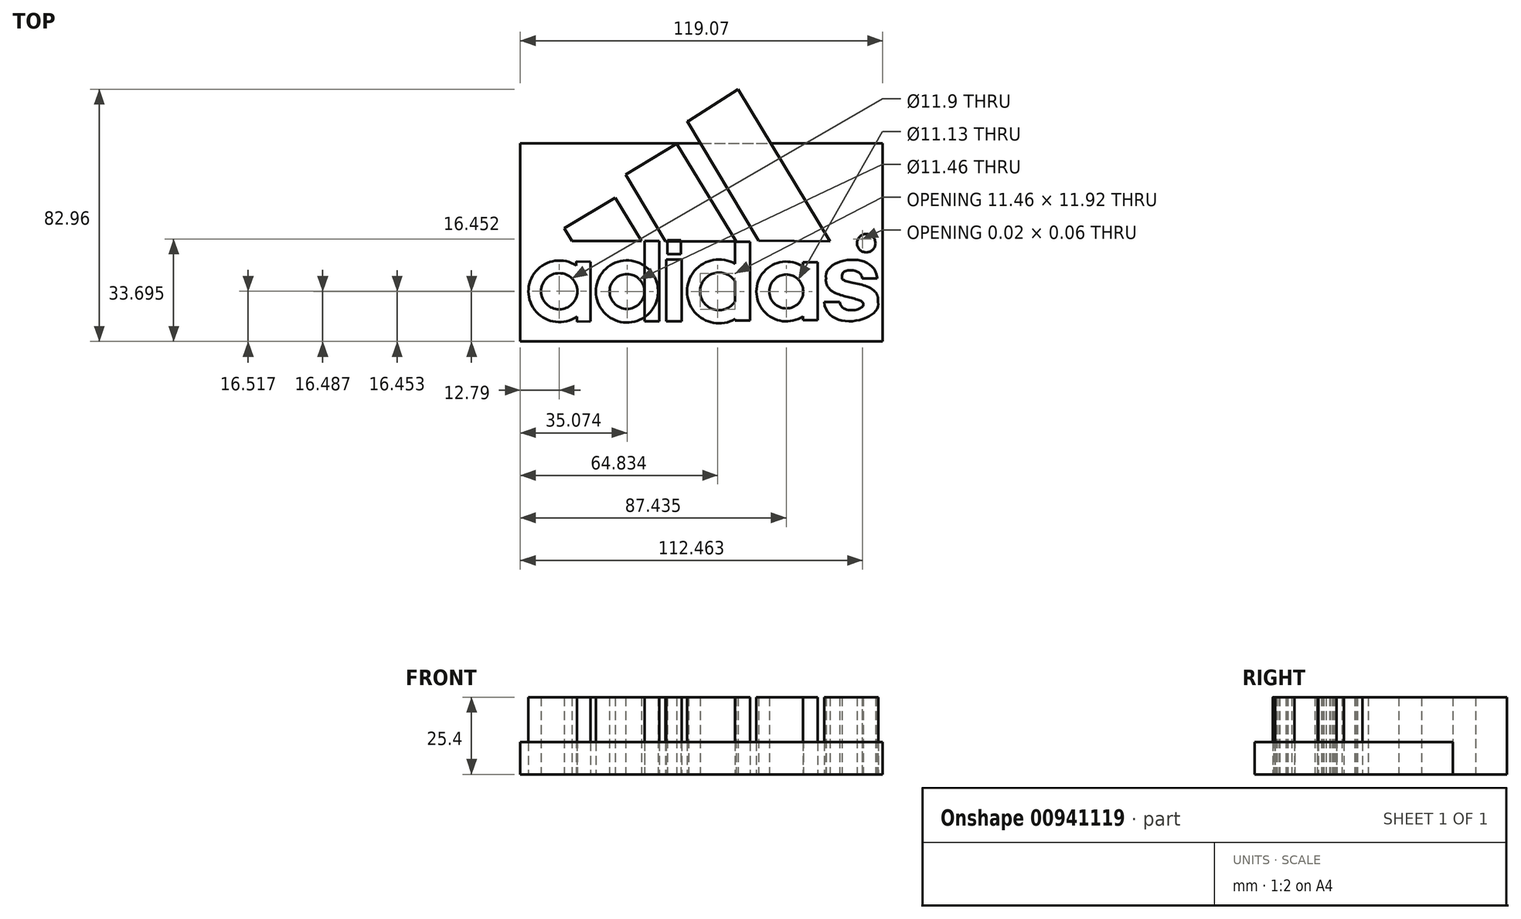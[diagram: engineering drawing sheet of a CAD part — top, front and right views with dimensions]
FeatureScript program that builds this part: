
annotation { "Feature Type Name" : "Feature", "Feature Type Description" : "" }
export const myFeature = defineFeature(function(context is Context, id is Id, definition is map)
    precondition{}
    {
        {
            var Q0;
            Q0=qCreatedBy(makeId("Top.planeOp"),FACE);
            var sketch = newSketch(context, id + "F0", { "sketchPlane" : qUnion([Q0])});
            skLineSegment(sketch, "E0", {"start": v(-39.48, 7.07) * mm, "end": v(-36.94, 2.8) * mm});
            skLineSegment(sketch, "E1", {"start": v(-36.94, 2.8) * mm, "end": v(-14.13, 2.8) * mm});
            skLineSegment(sketch, "E2", {"start": v(-14.13, 2.8) * mm, "end": v(-22.77, 17.1) * mm});
            skCircle(sketch, "E3", {"center": v(-41.14, -13.7) * mm, "radius": 10.12 * mm});
            skCircle(sketch, "E4", {"center": v(-18.86, -13.76) * mm, "radius": 10.22 * mm});
            skLineSegment(sketch, "E5", {"start": v(-22.77, 17.1) * mm, "end": v(-39.48, 7.07) * mm});
            skLineSegment(sketch, "E6", {"start": v(-19.29, 24.7) * mm, "end": v(-6.25, 2.78) * mm});
            skLineSegment(sketch, "E7", {"start": v(-6.25, 2.78) * mm, "end": v(16.96, 2.78) * mm});
            skLineSegment(sketch, "E8", {"start": v(16.96, 2.78) * mm, "end": v(-2.5, 34.87) * mm});
            skLineSegment(sketch, "E9", {"start": v(-2.5, 34.87) * mm, "end": v(-19.29, 24.7) * mm});
            skLineSegment(sketch, "E10", {"start": v(0.86, 42.38) * mm, "end": v(24.36, 2.98) * mm});
            skLineSegment(sketch, "E11", {"start": v(24.36, 2.98) * mm, "end": v(47.87, 2.68) * mm});
            skLineSegment(sketch, "E12", {"start": v(47.87, 2.68) * mm, "end": v(17.65, 52.75) * mm});
            skLineSegment(sketch, "E13", {"start": v(17.65, 52.75) * mm, "end": v(1.35, 42.38) * mm});
            skLineSegment(sketch, "E14", {"start": v(-13.03, -23.52) * mm, "end": v(-13.03, 2.8) * mm});
            skLineSegment(sketch, "E15", {"start": v(-13.03, 2.8) * mm, "end": v(-8.21, 2.8) * mm});
            skLineSegment(sketch, "E16", {"start": v(-8.21, 2.8) * mm, "end": v(-8.21, -23.6) * mm});
            skLineSegment(sketch, "E17", {"start": v(-8.21, -23.6) * mm, "end": v(-13.03, -23.52) * mm});
            skLineSegment(sketch, "E18", {"start": v(-35.53, -3.92) * mm, "end": v(-30.88, -4) * mm});
            skLineSegment(sketch, "E19", {"start": v(-30.88, -4) * mm, "end": v(-30.88, -23.52) * mm});
            skLineSegment(sketch, "E20", {"start": v(-30.88, -23.52) * mm, "end": v(-35.36, -23.65) * mm});
            skLineSegment(sketch, "E21", {"start": v(-35.36, -23.65) * mm, "end": v(-35.53, -3.92) * mm});
            skCircle(sketch, "E22", {"center": v(11.37, -13.72) * mm, "radius": 10.5 * mm});
            skLineSegment(sketch, "E23.bottom", {"start": v(21.61, 2.66) * mm, "end": v(16.63, 2.66) * mm});
            skLineSegment(sketch, "E23.top", {"start": v(21.61, -23.35) * mm, "end": v(16.63, -23.35) * mm});
            skLineSegment(sketch, "E23.left", {"start": v(21.61, 2.66) * mm, "end": v(21.61, -23.35) * mm});
            skLineSegment(sketch, "E23.right", {"start": v(16.63, 2.66) * mm, "end": v(16.63, -23.35) * mm});
            skCircle(sketch, "E24", {"center": v(33.5, -13.76) * mm, "radius": 9.83 * mm});
            skLineSegment(sketch, "E25.bottom", {"start": v(43.8, -4.13) * mm, "end": v(39, -4.13) * mm});
            skLineSegment(sketch, "E25.top", {"start": v(43.8, -23.18) * mm, "end": v(39, -23.18) * mm});
            skLineSegment(sketch, "E25.left", {"start": v(43.8, -4.13) * mm, "end": v(43.8, -23.18) * mm});
            skLineSegment(sketch, "E25.right", {"start": v(39, -4.13) * mm, "end": v(39, -23.18) * mm});
            skLineSegment(sketch, "E26.bottom", {"start": v(-5.57, 3.16) * mm, "end": v(-1.1, 3.16) * mm});
            skLineSegment(sketch, "E26.top", {"start": v(-5.57, -1.48) * mm, "end": v(-1.1, -1.48) * mm});
            skLineSegment(sketch, "E26.left", {"start": v(-5.57, 3.16) * mm, "end": v(-5.57, -1.48) * mm});
            skLineSegment(sketch, "E26.right", {"start": v(-1.1, 3.16) * mm, "end": v(-1.1, -1.48) * mm});
            skFitSpline(sketch, "E27", {"points": [v(63.31, -9.23) * mm, v(46.55, -9.6) * mm], "startDerivative": vector(-1.82, 27.46) * mm, "endDerivative": vector(4.32, -20.97) * mm});
            skFitSpline(sketch, "E28", {"points": [v(46.55, -9.6) * mm, v(58.8, -18) * mm], "startDerivative": vector(-1.87, -20.55) * mm, "endDerivative": vector(-0.15, -8.89) * mm});
            skFitSpline(sketch, "E29", {"points": [v(58.8, -18) * mm, v(51.07, -17.18) * mm], "startDerivative": vector(-0.5, -6.81) * mm, "endDerivative": vector(-0.92, 11.9) * mm});
            skLineSegment(sketch, "E30", {"start": v(51.07, -17.18) * mm, "end": v(45.92, -17.18) * mm});
            skFitSpline(sketch, "E31", {"points": [v(45.92, -17.18) * mm, v(63.62, -17.18) * mm], "startDerivative": vector(3.22, -31.3) * mm, "endDerivative": vector(-5.1, 18.8) * mm});
            skFitSpline(sketch, "E32", {"points": [v(63.62, -17.18) * mm, v(51.81, -9.24) * mm], "startDerivative": vector(2.68, 21.03) * mm, "endDerivative": vector(0.68, 6.95) * mm});
            skFitSpline(sketch, "E33", {"points": [v(51.81, -9.24) * mm, v(58.4, -9.48) * mm], "startDerivative": vector(-2.42, 10.76) * mm, "endDerivative": vector(-0.35, -10.04) * mm});
            skLineSegment(sketch, "E34", {"start": v(58.4, -9.48) * mm, "end": v(63.31, -9.48) * mm});
            skCircle(sketch, "E35", {"center": v(-41.14, -13.7) * mm, "radius": 5.95 * mm});
            skCircle(sketch, "E36", {"center": v(-61.96, 49.8) * mm, "radius": 8.9 * mm});
            skCircle(sketch, "E37", {"center": v(-18.86, -13.76) * mm, "radius": 5.73 * mm});
            skCircle(sketch, "E38", {"center": v(11.37, -13.72) * mm, "radius": 6.2 * mm});
            skCircle(sketch, "E39", {"center": v(33.5, -13.76) * mm, "radius": 5.57 * mm});
            skLineSegment(sketch, "E40", {"start": v(-41.14, -13.7) * mm, "end": v(73.81, -13.76) * mm});
            skLineSegment(sketch, "E41.bottom", {"start": v(-5.96, -3.28) * mm, "end": v(-0.9, -3.28) * mm});
            skLineSegment(sketch, "E41.top", {"start": v(-5.96, -23.55) * mm, "end": v(-0.9, -23.55) * mm});
            skLineSegment(sketch, "E41.left", {"start": v(-5.96, -3.28) * mm, "end": v(-5.96, -23.55) * mm});
            skLineSegment(sketch, "E41.right", {"start": v(-0.9, -3.28) * mm, "end": v(-0.9, -23.55) * mm});
            skCircle(sketch, "E42", {"center": v(59.77, 2.13) * mm, "radius": 3.03 * mm});
            skLineSegment(sketch, "E43", {"start": v(58.54, 0.35) * mm, "end": v(58.54, 3.52) * mm});
            skFitSpline(sketch, "E44", {"points": [v(58.54, 3.52) * mm, v(61.1, 2.56) * mm], "startDerivative": vector(-0.9, -0.98) * mm, "endDerivative": vector(-0.71, -4.78) * mm});
            skFitSpline(sketch, "E45", {"points": [v(61.1, 2.56) * mm, v(60.32, 1.72) * mm], "startDerivative": vector(-0.12, -0.78) * mm, "endDerivative": vector(-1.35, -0.31) * mm});
            skLineSegment(sketch, "E46", {"start": v(60.32, 1.72) * mm, "end": v(61.34, 0.36) * mm});
            skLineSegment(sketch, "E47", {"start": v(61.34, 0.36) * mm, "end": v(60.62, 0.36) * mm});
            skLineSegment(sketch, "E48", {"start": v(60.62, 0.36) * mm, "end": v(59.84, 1.57) * mm});
            skLineSegment(sketch, "E49", {"start": v(59.84, 1.57) * mm, "end": v(59.1, 1.57) * mm});
            skLineSegment(sketch, "E50", {"start": v(59.1, 1.57) * mm, "end": v(59.1, 0.34) * mm});
            skLineSegment(sketch, "E51", {"start": v(59.1, 0.34) * mm, "end": v(58.54, 0.35) * mm});
            skLineSegment(sketch, "E52", {"start": v(59.18, 2.97) * mm, "end": v(59.18, 2.3) * mm});
            skLineSegment(sketch, "E53", {"start": v(59.18, 2.3) * mm, "end": v(60.21, 2.3) * mm});
            skFitSpline(sketch, "E54", {"points": [v(60.21, 2.3) * mm, v(60.21, 2.98) * mm], "startDerivative": vector(0.84, 0.17) * mm, "endDerivative": vector(-1.16, 0.41) * mm});
            skLineSegment(sketch, "E55", {"start": v(59.18, 2.97) * mm, "end": v(60.21, 2.98) * mm});
            skLineSegment(sketch, "E56", {"start": v(63.31, -9.23) * mm, "end": v(63.31, -9.48) * mm});
            skLineSegment(sketch, "E57", {"start": v(1.35, 42.38) * mm, "end": v(0.86, 42.38) * mm});
            skSolve(sketch);
        }
        {
            var Q0;
            {var subQ0=sQuery(id+"F0.wireOp",EDGE,"E20");Q0=makeQuery(id+"F0.imprint","IMPRINT",FACE,{"disambiguationData":[TD([[makeQuery(id+"F0.imprint","IMPRINT",EDGE,{"derivedFrom":subQ0}),-1.0]])]});}
            var Q1;
            {var subQ0=sQuery(id+"F0.wireOp",EDGE,"E40");var subQ1=sQuery(id+"F0.wireOp",EDGE,"E4");var subQ2=makeQuery(id+"F0.imprint","INTERSECT",VERTEX,{"disambiguationData":[OD(0.0)],"derivedFrom":[subQ1,subQ0]});Q1=makeQuery(id+"F0.imprint","IMPRINT",FACE,{"disambiguationData":[TD([[makeQuery(id+"F0.imprint","IMPRINT",EDGE,{"disambiguationData":[TD([[subQ2,-1.0]])],"derivedFrom":subQ1}),1.0]])]});}
            var Q2;
            {var subQ5=sQuery(id+"F0.wireOp",EDGE,"E41.top");Q2=makeQuery(id+"F0.imprint","IMPRINT",FACE,{"disambiguationData":[TD([[makeQuery(id+"F0.imprint","IMPRINT",EDGE,{"derivedFrom":subQ5}),1.0]])]});}
            var Q3;
            {var subQ5=sQuery(id+"F0.wireOp",EDGE,"E41.bottom");Q3=makeQuery(id+"F0.imprint","IMPRINT",FACE,{"disambiguationData":[TD([[makeQuery(id+"F0.imprint","IMPRINT",EDGE,{"derivedFrom":subQ5}),-1.0]])]});}
            var Q4;
            {var subQ5=sQuery(id+"F0.wireOp",EDGE,"E26.top");Q4=makeQuery(id+"F0.imprint","IMPRINT",FACE,{"disambiguationData":[TD([[makeQuery(id+"F0.imprint","IMPRINT",EDGE,{"derivedFrom":subQ5}),1.0]])]});}
            var Q5;
            {var subQ0=sQuery(id+"F0.wireOp",EDGE,"E40");var subQ1=sQuery(id+"F0.wireOp",EDGE,"E22");var subQ2=makeQuery(id+"F0.imprint","INTERSECT",VERTEX,{"disambiguationData":[OD(0.0)],"derivedFrom":[subQ1,subQ0]});Q5=makeQuery(id+"F0.imprint","IMPRINT",FACE,{"disambiguationData":[TD([[makeQuery(id+"F0.imprint","IMPRINT",EDGE,{"disambiguationData":[TD([[subQ2,1.0]])],"derivedFrom":subQ1}),1.0]])]});}
            var Q6;
            {var subQ0=sQuery(id+"F0.wireOp",EDGE,"E40");var subQ1=sQuery(id+"F0.wireOp",EDGE,"E22");var subQ2=makeQuery(id+"F0.imprint","INTERSECT",VERTEX,{"disambiguationData":[OD(0.0)],"derivedFrom":[subQ1,subQ0]});Q6=makeQuery(id+"F0.imprint","IMPRINT",FACE,{"disambiguationData":[TD([[makeQuery(id+"F0.imprint","IMPRINT",EDGE,{"disambiguationData":[TD([[subQ2,-1.0]])],"derivedFrom":subQ1}),1.0]])]});}
            var Q7;
            {var subQ1=sQuery(id+"F0.wireOp",EDGE,"E23.right");var subQ5=sQuery(id+"F0.wireOp",EDGE,"E22");var subQ6=makeQuery(id+"F0.imprint","INTERSECT",VERTEX,{"disambiguationData":[OD(1.0)],"derivedFrom":[subQ5,subQ1]});Q7=makeQuery(id+"F0.imprint","IMPRINT",FACE,{"disambiguationData":[TD([[makeQuery(id+"F0.imprint","IMPRINT",EDGE,{"disambiguationData":[TD([[subQ6,-1.0]])],"derivedFrom":subQ5}),1.0]])]});}
            var Q8;
            {var subQ1=sQuery(id+"F0.wireOp",EDGE,"E23.right");var subQ5=sQuery(id+"F0.wireOp",EDGE,"E22");var subQ6=makeQuery(id+"F0.imprint","INTERSECT",VERTEX,{"disambiguationData":[OD(0.0)],"derivedFrom":[subQ5,subQ1]});Q8=makeQuery(id+"F0.imprint","IMPRINT",FACE,{"disambiguationData":[TD([[makeQuery(id+"F0.imprint","IMPRINT",EDGE,{"disambiguationData":[TD([[subQ6,1.0]])],"derivedFrom":subQ5}),1.0]])]});}
            var Q9;
            {var subQ5=sQuery(id+"F0.wireOp",EDGE,"E23.bottom");Q9=makeQuery(id+"F0.imprint","IMPRINT",FACE,{"disambiguationData":[TD([[makeQuery(id+"F0.imprint","IMPRINT",EDGE,{"derivedFrom":subQ5}),1.0]])]});}
            var Q10;
            {var subQ5=sQuery(id+"F0.wireOp",EDGE,"E23.top");Q10=makeQuery(id+"F0.imprint","IMPRINT",FACE,{"disambiguationData":[TD([[makeQuery(id+"F0.imprint","IMPRINT",EDGE,{"derivedFrom":subQ5}),-1.0]])]});}
            var Q11;
            {var subQ0=sQuery(id+"F0.wireOp",EDGE,"E38");var subQ1=sQuery(id+"F0.wireOp",EDGE,"E23.right");var subQ2=makeQuery(id+"F0.imprint","INTERSECT",VERTEX,{"disambiguationData":[OD(0.0)],"derivedFrom":[subQ1,subQ0]});Q11=makeQuery(id+"F0.imprint","IMPRINT",FACE,{"disambiguationData":[TD([[makeQuery(id+"F0.imprint","IMPRINT",EDGE,{"disambiguationData":[TD([[subQ2,-1.0]])],"derivedFrom":subQ1}),1.0]])]});}
            var Q12;
            {var subQ0=sQuery(id+"F0.wireOp",EDGE,"E40");var subQ1=sQuery(id+"F0.wireOp",EDGE,"E23.right");var subQ2=makeQuery(id+"F0.imprint","INTERSECT",VERTEX,{"derivedFrom":[subQ1,subQ0]});Q12=makeQuery(id+"F0.imprint","IMPRINT",FACE,{"disambiguationData":[TD([[makeQuery(id+"F0.imprint","IMPRINT",EDGE,{"disambiguationData":[TD([[subQ2,-1.0]])],"derivedFrom":subQ1}),1.0]])]});}
            var Q13;
            {var subQ0=sQuery(id+"F0.wireOp",EDGE,"E40");var subQ1=sQuery(id+"F0.wireOp",EDGE,"E24");var subQ2=makeQuery(id+"F0.imprint","INTERSECT",VERTEX,{"disambiguationData":[OD(0.0)],"derivedFrom":[subQ1,subQ0]});Q13=makeQuery(id+"F0.imprint","IMPRINT",FACE,{"disambiguationData":[TD([[makeQuery(id+"F0.imprint","IMPRINT",EDGE,{"disambiguationData":[TD([[subQ2,1.0]])],"derivedFrom":subQ1}),1.0]])]});}
            var Q14;
            {var subQ0=sQuery(id+"F0.wireOp",EDGE,"E25.right");var subQ1=sQuery(id+"F0.wireOp",EDGE,"E24");var subQ2=makeQuery(id+"F0.imprint","INTERSECT",VERTEX,{"disambiguationData":[OD(0.0)],"derivedFrom":[subQ1,subQ0]});Q14=makeQuery(id+"F0.imprint","IMPRINT",FACE,{"disambiguationData":[TD([[makeQuery(id+"F0.imprint","IMPRINT",EDGE,{"disambiguationData":[TD([[subQ2,1.0]])],"derivedFrom":subQ1}),1.0]])]});}
            var Q15;
            {var subQ0=sQuery(id+"F0.wireOp",EDGE,"E25.right");var subQ1=sQuery(id+"F0.wireOp",EDGE,"E24");var subQ2=makeQuery(id+"F0.imprint","INTERSECT",VERTEX,{"disambiguationData":[OD(1.0)],"derivedFrom":[subQ1,subQ0]});Q15=makeQuery(id+"F0.imprint","IMPRINT",FACE,{"disambiguationData":[TD([[makeQuery(id+"F0.imprint","IMPRINT",EDGE,{"disambiguationData":[TD([[subQ2,-1.0]])],"derivedFrom":subQ1}),1.0]])]});}
            var Q16;
            {var subQ0=sQuery(id+"F0.wireOp",EDGE,"E40");var subQ1=sQuery(id+"F0.wireOp",EDGE,"E24");var subQ2=makeQuery(id+"F0.imprint","INTERSECT",VERTEX,{"disambiguationData":[OD(0.0)],"derivedFrom":[subQ1,subQ0]});Q16=makeQuery(id+"F0.imprint","IMPRINT",FACE,{"disambiguationData":[TD([[makeQuery(id+"F0.imprint","IMPRINT",EDGE,{"disambiguationData":[TD([[subQ2,-1.0]])],"derivedFrom":subQ1}),1.0]])]});}
            var Q17;
            {var subQ1=sQuery(id+"F0.wireOp",EDGE,"E25.top");Q17=makeQuery(id+"F0.imprint","IMPRINT",FACE,{"disambiguationData":[TD([[makeQuery(id+"F0.imprint","IMPRINT",EDGE,{"derivedFrom":subQ1}),-1.0]])]});}
            var Q18;
            {var subQ1=sQuery(id+"F0.wireOp",EDGE,"E25.bottom");Q18=makeQuery(id+"F0.imprint","IMPRINT",FACE,{"disambiguationData":[TD([[makeQuery(id+"F0.imprint","IMPRINT",EDGE,{"derivedFrom":subQ1}),1.0]])]});}
            var Q19;
            {var subQ1=sQuery(id+"F0.wireOp",EDGE,"E29");Q19=makeQuery(id+"F0.imprint","IMPRINT",FACE,{"disambiguationData":[TD([[makeQuery(id+"F0.imprint","IMPRINT",EDGE,{"derivedFrom":subQ1}),1.0]])]});}
            var Q20;
            {var subQ7=sQuery(id+"F0.wireOp",EDGE,"E6");Q20=makeQuery(id+"F0.imprint","IMPRINT",FACE,{"disambiguationData":[TD([[makeQuery(id+"F0.imprint","IMPRINT",EDGE,{"derivedFrom":subQ7}),1.0]])]});}
            var Q21;
            Q21=makeQuery(id+"F0.imprint","IMPRINT",FACE,{"disambiguationData":[TD([[makeQuery(id+"F0.imprint","IMPRINT",EDGE,{"derivedFrom":sQuery(id+"F0.wireOp",EDGE,"E0")}),1.0]])]});
            var Q22;
            Q22=makeQuery(id+"F0.imprint","IMPRINT",FACE,{"disambiguationData":[TD([[makeQuery(id+"F0.imprint","IMPRINT",EDGE,{"derivedFrom":sQuery(id+"F0.wireOp",EDGE,"E52")}),1.0]])]});
            var Q23;
            {var subQ5=sQuery(id+"F0.wireOp",EDGE,"E27");Q23=makeQuery(id+"F0.imprint","IMPRINT",FACE,{"disambiguationData":[TD([[makeQuery(id+"F0.imprint","IMPRINT",EDGE,{"derivedFrom":subQ5}),1.0]])]});}
            var Q24;
            Q24=makeQuery(id+"F0.imprint","IMPRINT",FACE,{"disambiguationData":[TD([[makeQuery(id+"F0.imprint","IMPRINT",EDGE,{"derivedFrom":sQuery(id+"F0.wireOp",EDGE,"E10")}),1.0]])]});
            var Q25;
            {var subQ0=sQuery(id+"F0.wireOp",EDGE,"E21");var subQ1=sQuery(id+"F0.wireOp",EDGE,"E3");var subQ2=makeQuery(id+"F0.imprint","INTERSECT",VERTEX,{"disambiguationData":[OD(0.0)],"derivedFrom":[subQ1,subQ0]});Q25=makeQuery(id+"F0.imprint","IMPRINT",FACE,{"disambiguationData":[TD([[makeQuery(id+"F0.imprint","IMPRINT",EDGE,{"disambiguationData":[TD([[subQ2,1.0]])],"derivedFrom":subQ1}),1.0]])]});}
            var Q26;
            {var subQ0=sQuery(id+"F0.wireOp",EDGE,"E21");var subQ1=sQuery(id+"F0.wireOp",EDGE,"E3");var subQ2=makeQuery(id+"F0.imprint","INTERSECT",VERTEX,{"disambiguationData":[OD(1.0)],"derivedFrom":[subQ1,subQ0]});Q26=makeQuery(id+"F0.imprint","IMPRINT",FACE,{"disambiguationData":[TD([[makeQuery(id+"F0.imprint","IMPRINT",EDGE,{"disambiguationData":[TD([[subQ2,1.0]])],"derivedFrom":subQ1}),1.0]])]});}
            var Q27;
            {var subQ0=sQuery(id+"F0.wireOp",EDGE,"E21");var subQ1=sQuery(id+"F0.wireOp",EDGE,"E3");var subQ2=makeQuery(id+"F0.imprint","INTERSECT",VERTEX,{"disambiguationData":[OD(0.0)],"derivedFrom":[subQ1,subQ0]});Q27=makeQuery(id+"F0.imprint","IMPRINT",FACE,{"disambiguationData":[TD([[makeQuery(id+"F0.imprint","IMPRINT",EDGE,{"disambiguationData":[TD([[subQ2,-1.0]])],"derivedFrom":subQ1}),1.0]])]});}
            var Q28;
            {var subQ0=sQuery(id+"F0.wireOp",EDGE,"E14");var subQ1=sQuery(id+"F0.wireOp",EDGE,"E4");var subQ2=makeQuery(id+"F0.imprint","INTERSECT",VERTEX,{"disambiguationData":[OD(1.0)],"derivedFrom":[subQ1,subQ0]});Q28=makeQuery(id+"F0.imprint","IMPRINT",FACE,{"disambiguationData":[TD([[makeQuery(id+"F0.imprint","IMPRINT",EDGE,{"disambiguationData":[TD([[subQ2,-1.0]])],"derivedFrom":subQ1}),1.0]])]});}
            var Q29;
            {var subQ0=sQuery(id+"F0.wireOp",EDGE,"E17");Q29=makeQuery(id+"F0.imprint","IMPRINT",FACE,{"disambiguationData":[TD([[makeQuery(id+"F0.imprint","IMPRINT",EDGE,{"derivedFrom":subQ0}),-1.0]])]});}
            var Q30;
            {var subQ0=sQuery(id+"F0.wireOp",EDGE,"E15");Q30=makeQuery(id+"F0.imprint","IMPRINT",FACE,{"disambiguationData":[TD([[makeQuery(id+"F0.imprint","IMPRINT",EDGE,{"derivedFrom":subQ0}),-1.0]])]});}
            var Q31;
            {var subQ0=sQuery(id+"F0.wireOp",EDGE,"E40");var subQ1=sQuery(id+"F0.wireOp",EDGE,"E4");var subQ2=makeQuery(id+"F0.imprint","INTERSECT",VERTEX,{"disambiguationData":[OD(0.0)],"derivedFrom":[subQ1,subQ0]});Q31=makeQuery(id+"F0.imprint","IMPRINT",FACE,{"disambiguationData":[TD([[makeQuery(id+"F0.imprint","IMPRINT",EDGE,{"disambiguationData":[TD([[subQ2,1.0]])],"derivedFrom":subQ1}),1.0]])]});}
            var Q32;
            {var subQ4=sQuery(id+"F0.wireOp",EDGE,"E45");Q32=makeQuery(id+"F0.imprint","IMPRINT",FACE,{"disambiguationData":[TD([[makeQuery(id+"F0.imprint","IMPRINT",EDGE,{"derivedFrom":subQ4}),-1.0]])]});}
            var Q33;
            Q33=makeQuery(id+"F0.imprint","IMPRINT",FACE,{"disambiguationData":[TD([[makeQuery(id+"F0.imprint","IMPRINT",EDGE,{"derivedFrom":sQuery(id+"F0.wireOp",EDGE,"E42")}),1.0]])]});
            var Q34;
            {var subQ0=sQuery(id+"F0.wireOp",EDGE,"E14");var subQ1=sQuery(id+"F0.wireOp",EDGE,"E4");var subQ2=makeQuery(id+"F0.imprint","INTERSECT",VERTEX,{"disambiguationData":[OD(0.0)],"derivedFrom":[subQ1,subQ0]});Q34=makeQuery(id+"F0.imprint","IMPRINT",FACE,{"disambiguationData":[TD([[makeQuery(id+"F0.imprint","IMPRINT",EDGE,{"disambiguationData":[TD([[subQ2,1.0]])],"derivedFrom":subQ1}),1.0]])]});}
            var Q35;
            {var subQ1=sQuery(id+"F0.wireOp",EDGE,"E18");Q35=makeQuery(id+"F0.imprint","IMPRINT",FACE,{"disambiguationData":[TD([[makeQuery(id+"F0.imprint","IMPRINT",EDGE,{"derivedFrom":subQ1}),-1.0]])]});}
            extrude(context, id + "F1", {"entities" : qUnion([Q0, Q1, Q2, Q3, Q4, Q5, Q6, Q7, Q8, Q9, Q10, Q11, Q12, Q13, Q14, Q15, Q16, Q17, Q18, Q19, Q20, Q21, Q22, Q23, Q24, Q25, Q26, Q27, Q28, Q29, Q30, Q31, Q32, Q33, Q34, Q35]), "depth" : 25.4 * mm, "offsetDistance" : 25.4 * mm});
        }
        {
            var Q0;
            Q0=qCreatedBy(makeId("Top.planeOp"),FACE);
            var sketch = newSketch(context, id + "F2", { "sketchPlane" : qUnion([Q0])});
            skLineSegment(sketch, "E58.bottom", {"start": v(-53.93, -30.2) * mm, "end": v(65.14, -30.2) * mm});
            skLineSegment(sketch, "E58.top", {"start": v(-53.93, 34.98) * mm, "end": v(65.14, 34.98) * mm});
            skLineSegment(sketch, "E58.left", {"start": v(-53.93, -30.2) * mm, "end": v(-53.93, 34.98) * mm});
            skLineSegment(sketch, "E58.right", {"start": v(65.14, -30.2) * mm, "end": v(65.14, 34.98) * mm});
            skSolve(sketch);
        }
        {
            var Q0;
            Q0=makeQuery(id+"F2.imprint","IMPRINT",FACE,{"disambiguationData":[TD([[makeQuery(id+"F2.imprint","IMPRINT",EDGE,{"derivedFrom":sQuery(id+"F2.wireOp",EDGE,"E58.bottom")}),1.0]])]});
            extrude(context, id + "F3", {"entities" : qUnion([Q0]), "depth" : 10.67 * mm, "offsetDistance" : 25.4 * mm});
        }
    });
